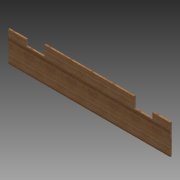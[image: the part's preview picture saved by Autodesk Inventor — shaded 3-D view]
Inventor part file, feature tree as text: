
AUTODESK INVENTOR PART (.ipt)
format: ipt  version: 2012 (Build 160160000, 160)  size: 94,720 bytes
history: native  units: in
note: dims shown in document units (in); Inventor stores cm internally (conversion verified against a paired STEP export)
features: extrude x1, sketch x1
ambient origin geometry x8: Origin, YZ Plane, XZ Plane, XY Plane, X Axis, Y Axis, Z Axis, Center Point
bodies: Solid1 (feature_tree)
feature tree (2):
  extrude  "Extrusion1"  Depth=27.0in
  sketch  "Sketch1"  dims[d0=5.0in d1=27.0in d2=0.25in d3=0.0in d4=3.0in d6=3.0in d7=3.0in d8=3.0in d10=1.0in d11=1.75in d12=1.0in]
